# Revit family: QF_Pratica_Chef Express_Speed Oven_Fit Life_EN
name_source: partatom
category: Specialty Equipment
units: mm (PartAtom-declared; Revit-internal decimal feet)

## family parameters
Always vertical = Yes
Cut with Voids When Loaded = No
Enable Cutting in Views = No
Maintain Annotation Orientation = No
OmniClass Number = 23.40.40.14.17.11
OmniClass Title = Cookers, Ovens, Stoves
Part Type = Normal
Room Calculation Point = No
Round Connector Dimension = Use Diameter
Shared = No
Work Plane-Based = No

## types (1)
- Fit Express USA - Black (230/1/50)
    Cable = 3x2,5mm²
    Capacity = 13 L
    Circuit Breaker = 13A
    Conn Plug = 13A (2P+E)
    Cycle = 50 Hz
    Default Elevation = 0 "
    Depth = 27 "
    Description = The Fit Lite oven is intended for the rapid finishing of refrigerated foods, pre-fried savory items, pre-baked products, lasagnas, pasta, sandwiches, casseroles, and 
other semi-prepared foods, delivering excellent results in flavor, appearance, and crispness. The impinged air convection technology combined with microwave energy allows food to be heated, gratinated, or toasted.
    Details = QF_Metal_Stainless Steel
    Developer = Blocks
    Developer URL = https://www.BlocksRvt.com
    Door = QF_Metal_Stainless Steel
    Height = 24 "
    Logo = QF_Plastic_Gray_Matte
    Manufacturer = Pratica USA
    Model = Fit Lite
    Number of Poles = 1
    Panel = QF_Plastic_Black_Matte
    Phase = 1
    Specification by Manufacturer = The oven must be installed on a base or counter that supports the weight of the unit (approximately 123.4 lbs. / 56 kg). For proper ventilation, a minimum space of 0.8'' is required between the back of the oven and the wall. The bumper, located at the back of the oven, has been designed to provide this necessary space at the back of the oven and cannot be removed. Do not block the air inlets and outlets located on the front and back of the oven. It is not recommended for the unit to be positioned near stoves, deep fryers, hot plates and other equipment that releases fat, fumes and heat. The oven must be installed at a leveled and ventilated location.
Improper installation may void the equipment warranty.
    Structure = QF_Metal_Gray_Dark
    URL = https://praticausa.com
    Ventilation Offset Rear = 1 "
    Volts = 230 V
    Wall Clearance Service Offset Left = 0 "
    Wall Clearance Service Offset Rear = 0 "
    Wall Clearance Service Offset Right = 0 "
    Watts = 3300 W
    Weight in Pounds = 123.5
    Width = 15 "
